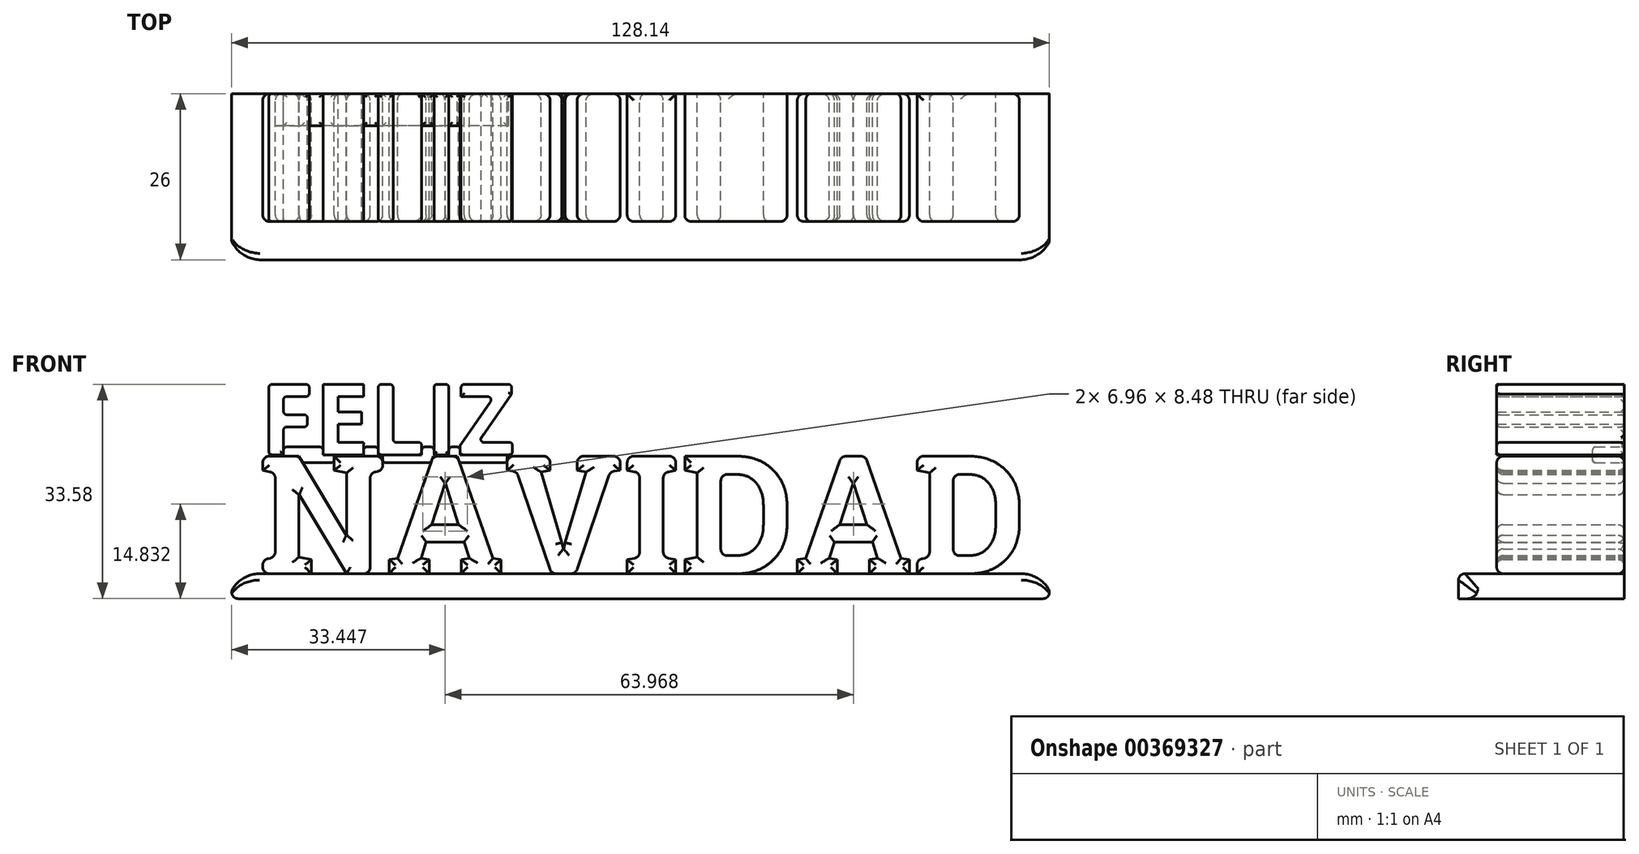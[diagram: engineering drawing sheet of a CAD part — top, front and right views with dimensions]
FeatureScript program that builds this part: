
annotation { "Feature Type Name" : "Feature", "Feature Type Description" : "" }
export const myFeature = defineFeature(function(context is Context, id is Id, definition is map)
    precondition{}
    {
        {
            var Q0;
            Q0=qCreatedBy(makeId("Front.planeOp"),FACE);
            var sketch = newSketch(context, id + "F0", { "sketchPlane" : qUnion([Q0])});
            skText(sketch, "E0", { "text": "NAVIDAD", "fontName": "RobotoSlab-Bold.ttf"});
            skText(sketch, "E1", { "text": "FELIZ", "fontName": "OpenSans-Bold.ttf"});
            skLineSegment(sketch, "E2.bottom", {"start": v(64.02, 0) * mm, "end": v(-65.06, 0) * mm});
            skLineSegment(sketch, "E2.top", {"start": v(64.02, -3.91) * mm, "end": v(-65.06, -3.91) * mm});
            skLineSegment(sketch, "E2.left", {"start": v(64.02, 0) * mm, "end": v(64.02, -3.91) * mm});
            skLineSegment(sketch, "E2.right", {"start": v(-65.06, 0) * mm, "end": v(-65.06, -3.91) * mm});
            skLineSegment(sketch, "E3.bottom", {"start": v(-21.18, 19.85) * mm, "end": v(-57.76, 19.85) * mm});
            skLineSegment(sketch, "E3.top", {"start": v(-21.18, 17.37) * mm, "end": v(-57.76, 17.37) * mm});
            skLineSegment(sketch, "E3.left", {"start": v(-21.18, 19.85) * mm, "end": v(-21.18, 17.37) * mm});
            skLineSegment(sketch, "E3.right", {"start": v(-57.76, 19.85) * mm, "end": v(-57.76, 17.37) * mm});
            const initialGuessF0  = {"E0": [-0.06043, 0, 1, 0, 0.01863], "E1": [-0.06016, 0.01863, 1, 0, 0.01113]};
            skSetInitialGuess(sketch, initialGuessF0);
            skSolve(sketch);
        }
        {
            var Q0;
            Q0=makeQuery(id+"F0.imprint","IMPRINT",FACE,{"disambiguationData":[TD([[makeQuery(id+"F0.imprint","IMPRINT",EDGE,{"derivedFrom":sQuery(id+"F0.wireOp",EDGE,"E0.sketch_text.stroke-115")}),-1.0]])]});
            var Q1;
            Q1=makeQuery(id+"F0.imprint","IMPRINT",FACE,{"disambiguationData":[TD([[makeQuery(id+"F0.imprint","IMPRINT",EDGE,{"derivedFrom":sQuery(id+"F0.wireOp",EDGE,"E0.sketch_text.stroke-95")}),-1.0]])]});
            var Q2;
            Q2=makeQuery(id+"F0.imprint","IMPRINT",FACE,{"disambiguationData":[TD([[makeQuery(id+"F0.imprint","IMPRINT",EDGE,{"derivedFrom":sQuery(id+"F0.wireOp",EDGE,"E0.sketch_text.stroke-74")}),-1.0]])]});
            var Q3;
            Q3=makeQuery(id+"F0.imprint","IMPRINT",FACE,{"disambiguationData":[TD([[makeQuery(id+"F0.imprint","IMPRINT",EDGE,{"derivedFrom":sQuery(id+"F0.wireOp",EDGE,"E0.sketch_text.stroke-62")}),-1.0]])]});
            var Q4;
            Q4=makeQuery(id+"F0.imprint","IMPRINT",FACE,{"disambiguationData":[TD([[makeQuery(id+"F0.imprint","IMPRINT",EDGE,{"derivedFrom":sQuery(id+"F0.wireOp",EDGE,"E0.sketch_text.stroke-44")}),-1.0]])]});
            var Q5;
            {var subQ7=sQuery(id+"F0.wireOp",EDGE,"E0.sketch_text.stroke-24");Q5=makeQuery(id+"F0.imprint","IMPRINT",FACE,{"disambiguationData":[TD([[makeQuery(id+"F0.imprint","IMPRINT",EDGE,{"derivedFrom":subQ7}),-1.0]])]});}
            var Q6;
            {var subQ16=sQuery(id+"F0.wireOp",EDGE,"E0.sketch_text.stroke-1");Q6=makeQuery(id+"F0.imprint","IMPRINT",FACE,{"disambiguationData":[TD([[makeQuery(id+"F0.imprint","IMPRINT",EDGE,{"derivedFrom":subQ16}),-1.0]])]});}
            var Q7;
            {var subQ4=sQuery(id+"F0.wireOp",EDGE,"E1.sketch_text.stroke-1");Q7=makeQuery(id+"F0.imprint","IMPRINT",FACE,{"disambiguationData":[TD([[makeQuery(id+"F0.imprint","IMPRINT",EDGE,{"derivedFrom":subQ4}),-1.0]])]});}
            var Q8;
            {var subQ0=sQuery(id+"F0.wireOp",EDGE,"E1.sketch_text.stroke-9");var subQ1=sQuery(id+"F0.wireOp",EDGE,"E1.sketch_text.stroke-0");var subQ2=makeQuery(id+"F0.imprint","INTERSECT",VERTEX,{"derivedFrom":[subQ1,subQ0]});Q8=makeQuery(id+"F0.imprint","IMPRINT",FACE,{"disambiguationData":[TD([[makeQuery(id+"F0.imprint","IMPRINT",EDGE,{"disambiguationData":[TD([[subQ2,-1.0]])],"derivedFrom":subQ1}),-1.0]])]});}
            var Q9;
            {var subQ0=sQuery(id+"F0.wireOp",EDGE,"E1.sketch_text.stroke-10");Q9=makeQuery(id+"F0.imprint","IMPRINT",FACE,{"disambiguationData":[TD([[makeQuery(id+"F0.imprint","IMPRINT",EDGE,{"derivedFrom":subQ0}),-1.0]])]});}
            var Q10;
            {var subQ1=sQuery(id+"F0.wireOp",EDGE,"E1.sketch_text.stroke-12");Q10=makeQuery(id+"F0.imprint","IMPRINT",FACE,{"disambiguationData":[TD([[makeQuery(id+"F0.imprint","IMPRINT",EDGE,{"derivedFrom":subQ1}),-1.0]])]});}
            var Q11;
            {var subQ1=sQuery(id+"F0.wireOp",EDGE,"E1.sketch_text.stroke-23");Q11=makeQuery(id+"F0.imprint","IMPRINT",FACE,{"disambiguationData":[TD([[makeQuery(id+"F0.imprint","IMPRINT",EDGE,{"derivedFrom":subQ1}),-1.0]])]});}
            var Q12;
            {var subQ0=sQuery(id+"F0.wireOp",EDGE,"E1.sketch_text.stroke-27");Q12=makeQuery(id+"F0.imprint","IMPRINT",FACE,{"disambiguationData":[TD([[makeQuery(id+"F0.imprint","IMPRINT",EDGE,{"derivedFrom":subQ0}),-1.0]])]});}
            var Q13;
            {var subQ0=sQuery(id+"F0.wireOp",EDGE,"E1.sketch_text.stroke-31");Q13=makeQuery(id+"F0.imprint","IMPRINT",FACE,{"disambiguationData":[TD([[makeQuery(id+"F0.imprint","IMPRINT",EDGE,{"derivedFrom":subQ0}),-1.0]])]});}
            var Q14;
            {var subQ0=sQuery(id+"F0.wireOp",EDGE,"E1.sketch_text.stroke-29");Q14=makeQuery(id+"F0.imprint","IMPRINT",FACE,{"disambiguationData":[TD([[makeQuery(id+"F0.imprint","IMPRINT",EDGE,{"derivedFrom":subQ0}),-1.0]])]});}
            var Q15;
            {var subQ0=sQuery(id+"F0.wireOp",EDGE,"E1.sketch_text.stroke-33");var subQ1=sQuery(id+"F0.wireOp",EDGE,"E1.sketch_text.stroke-32");var subQ2=makeQuery(id+"F0.imprint","INTERSECT",VERTEX,{"derivedFrom":[subQ1,subQ0]});Q15=makeQuery(id+"F0.imprint","IMPRINT",FACE,{"disambiguationData":[TD([[makeQuery(id+"F0.imprint","IMPRINT",EDGE,{"disambiguationData":[TD([[subQ2,1.0]])],"derivedFrom":subQ1}),-1.0]])]});}
            var Q16;
            {var subQ6=sQuery(id+"F0.wireOp",EDGE,"E1.sketch_text.stroke-34");Q16=makeQuery(id+"F0.imprint","IMPRINT",FACE,{"disambiguationData":[TD([[makeQuery(id+"F0.imprint","IMPRINT",EDGE,{"derivedFrom":subQ6}),-1.0]])]});}
            var Q17;
            {var subQ0=sQuery(id+"F0.wireOp",EDGE,"E0.sketch_text.stroke-60");var subQ1=sQuery(id+"F0.wireOp",EDGE,"E0.sketch_text.stroke-59");var subQ2=makeQuery(id+"F0.imprint","INTERSECT",VERTEX,{"derivedFrom":[subQ1,subQ0]});Q17=makeQuery(id+"F0.imprint","IMPRINT",FACE,{"disambiguationData":[TD([[makeQuery(id+"F0.imprint","IMPRINT",EDGE,{"disambiguationData":[TD([[subQ2,1.0]])],"derivedFrom":subQ1}),-1.0]])]});}
            var Q18;
            {var subQ0=sQuery(id+"F0.wireOp",EDGE,"E0.sketch_text.stroke-26");Q18=makeQuery(id+"F0.imprint","IMPRINT",FACE,{"disambiguationData":[TD([[makeQuery(id+"F0.imprint","IMPRINT",EDGE,{"derivedFrom":subQ0}),-1.0]])]});}
            var Q19;
            {var subQ0=sQuery(id+"F0.wireOp",EDGE,"E0.sketch_text.stroke-22");Q19=makeQuery(id+"F0.imprint","IMPRINT",FACE,{"disambiguationData":[TD([[makeQuery(id+"F0.imprint","IMPRINT",EDGE,{"derivedFrom":subQ0}),-1.0]])]});}
            var Q20;
            {var subQ0=sQuery(id+"F0.wireOp",EDGE,"E0.sketch_text.stroke-17");var subQ1=sQuery(id+"F0.wireOp",EDGE,"E0.sketch_text.stroke-16");var subQ2=makeQuery(id+"F0.imprint","INTERSECT",VERTEX,{"derivedFrom":[subQ1,subQ0]});Q20=makeQuery(id+"F0.imprint","IMPRINT",FACE,{"disambiguationData":[TD([[makeQuery(id+"F0.imprint","IMPRINT",EDGE,{"disambiguationData":[TD([[subQ2,1.0]])],"derivedFrom":subQ1}),-1.0]])]});}
            extrude(context, id + "F1", {"entities" : qUnion([Q0, Q1, Q2, Q3, Q4, Q5, Q6, Q7, Q8, Q9, Q10, Q11, Q12, Q13, Q14, Q15, Q16, Q17, Q18, Q19, Q20]), "depth" : 20 * mm});
        }
        {
            var Q0;
            {var subQ39=sQuery(id+"F0.wireOp",EDGE,"E0.sketch_text.stroke-22");Q0=makeQuery(id+"F0.imprint","IMPRINT",FACE,{"disambiguationData":[TD([[makeQuery(id+"F0.imprint","IMPRINT",EDGE,{"derivedFrom":subQ39}),1.0]])]});}
            extrude(context, id + "F2", {"entities" : qUnion([Q0]), "depth" : 5 * mm});
        }
        {
            var Q0;
            Q0=makeQuery(id+"F0.imprint","IMPRINT",FACE,{"disambiguationData":[TD([[makeQuery(id+"F0.imprint","IMPRINT",EDGE,{"derivedFrom":sQuery(id+"F0.wireOp",EDGE,"E2.top")}),-1.0]])]});
            extrude(context, id + "F3", {"entities" : qUnion([Q0]), "depth" : 26 * mm});
        }
        {
            var Q0;
            Q0=makeQuery(id+"F3.opExtrude","CAP_EDGE",EDGE,{"disambiguationData":[OSD([sQuery(id+"F0.wireOp",EDGE,"E2.right")])],"isStart":false});
            var Q1;
            Q1=makeQuery(id+"F3.opExtrude","SWEPT_EDGE",EDGE,{"disambiguationData":[OSD([sQuery(id+"F0.wireOp",EDGE,"E2.bottom"),sQuery(id+"F0.wireOp",EDGE,"E2.right")])]});
            var Q2;
            Q2=makeQuery(id+"F3.opExtrude","CAP_EDGE",EDGE,{"disambiguationData":[OSD([sQuery(id+"F0.wireOp",EDGE,"E2.left")])],"isStart":false});
            var Q3;
            Q3=makeQuery(id+"F3.opExtrude","SWEPT_EDGE",EDGE,{"disambiguationData":[OSD([sQuery(id+"F0.wireOp",EDGE,"E2.bottom"),sQuery(id+"F0.wireOp",EDGE,"E2.left")])]});
            fillet(context, id + "F4", {"entities" : qUnion([Q0, Q1, Q2, Q3]), "radius" : 5 * mm, "tangentPropagation" : true, "allowEdgeOverflow" : false});
        }
        {
            var Q0;
            Q0=makeQuery(id+"F1.opExtrude","CAP_FACE",FACE,{"disambiguationData":[OSD([sQuery(id+"F0.wireOp",EDGE,"E0.sketch_text.stroke-0"),sQuery(id+"F0.wireOp",EDGE,"E0.sketch_text.stroke-1"),sQuery(id+"F0.wireOp",EDGE,"E0.sketch_text.stroke-2"),sQuery(id+"F0.wireOp",EDGE,"E0.sketch_text.stroke-4"),sQuery(id+"F0.wireOp",EDGE,"E0.sketch_text.stroke-5"),sQuery(id+"F0.wireOp",EDGE,"E0.sketch_text.stroke-6"),sQuery(id+"F0.wireOp",EDGE,"E0.sketch_text.stroke-7"),sQuery(id+"F0.wireOp",EDGE,"E0.sketch_text.stroke-8"),sQuery(id+"F0.wireOp",EDGE,"E0.sketch_text.stroke-10"),sQuery(id+"F0.wireOp",EDGE,"E0.sketch_text.stroke-11"),sQuery(id+"F0.wireOp",EDGE,"E0.sketch_text.stroke-12"),sQuery(id+"F0.wireOp",EDGE,"E0.sketch_text.stroke-13"),sQuery(id+"F0.wireOp",EDGE,"E0.sketch_text.stroke-14"),sQuery(id+"F0.wireOp",EDGE,"E0.sketch_text.stroke-15"),sQuery(id+"F0.wireOp",EDGE,"E0.sketch_text.stroke-16"),sQuery(id+"F0.wireOp",EDGE,"E0.sketch_text.stroke-17"),sQuery(id+"F0.wireOp",EDGE,"E0.sketch_text.stroke-18"),sQuery(id+"F0.wireOp",EDGE,"E0.sketch_text.stroke-19"),sQuery(id+"F0.wireOp",EDGE,"E0.sketch_text.stroke-20"),sQuery(id+"F0.wireOp",EDGE,"E0.sketch_text.stroke-21"),sQuery(id+"F0.wireOp",EDGE,"E0.sketch_text.stroke-22"),sQuery(id+"F0.wireOp",EDGE,"E0.sketch_text.stroke-23"),sQuery(id+"F0.wireOp",EDGE,"E2.bottom")])],"isStart":false});
            var Q1;
            Q1=makeQuery(id+"F1.opExtrude","CAP_FACE",FACE,{"disambiguationData":[OSD([sQuery(id+"F0.wireOp",EDGE,"E0.sketch_text.stroke-24"),sQuery(id+"F0.wireOp",EDGE,"E0.sketch_text.stroke-25"),sQuery(id+"F0.wireOp",EDGE,"E0.sketch_text.stroke-26"),sQuery(id+"F0.wireOp",EDGE,"E0.sketch_text.stroke-27"),sQuery(id+"F0.wireOp",EDGE,"E0.sketch_text.stroke-28"),sQuery(id+"F0.wireOp",EDGE,"E0.sketch_text.stroke-29"),sQuery(id+"F0.wireOp",EDGE,"E0.sketch_text.stroke-31"),sQuery(id+"F0.wireOp",EDGE,"E0.sketch_text.stroke-32"),sQuery(id+"F0.wireOp",EDGE,"E0.sketch_text.stroke-33"),sQuery(id+"F0.wireOp",EDGE,"E0.sketch_text.stroke-34"),sQuery(id+"F0.wireOp",EDGE,"E0.sketch_text.stroke-35"),sQuery(id+"F0.wireOp",EDGE,"E0.sketch_text.stroke-36"),sQuery(id+"F0.wireOp",EDGE,"E0.sketch_text.stroke-37"),sQuery(id+"F0.wireOp",EDGE,"E0.sketch_text.stroke-39"),sQuery(id+"F0.wireOp",EDGE,"E0.sketch_text.stroke-40"),sQuery(id+"F0.wireOp",EDGE,"E0.sketch_text.stroke-41"),sQuery(id+"F0.wireOp",EDGE,"E0.sketch_text.stroke-42"),sQuery(id+"F0.wireOp",EDGE,"E0.sketch_text.stroke-43"),sQuery(id+"F0.wireOp",EDGE,"E2.bottom")])],"isStart":false});
            var Q2;
            Q2=makeQuery(id+"F1.opExtrude","CAP_FACE",FACE,{"disambiguationData":[OSD([sQuery(id+"F0.wireOp",EDGE,"E0.sketch_text.stroke-44"),sQuery(id+"F0.wireOp",EDGE,"E0.sketch_text.stroke-45"),sQuery(id+"F0.wireOp",EDGE,"E0.sketch_text.stroke-46"),sQuery(id+"F0.wireOp",EDGE,"E0.sketch_text.stroke-47"),sQuery(id+"F0.wireOp",EDGE,"E0.sketch_text.stroke-48"),sQuery(id+"F0.wireOp",EDGE,"E0.sketch_text.stroke-49"),sQuery(id+"F0.wireOp",EDGE,"E0.sketch_text.stroke-50"),sQuery(id+"F0.wireOp",EDGE,"E0.sketch_text.stroke-51"),sQuery(id+"F0.wireOp",EDGE,"E0.sketch_text.stroke-52"),sQuery(id+"F0.wireOp",EDGE,"E0.sketch_text.stroke-53"),sQuery(id+"F0.wireOp",EDGE,"E0.sketch_text.stroke-54"),sQuery(id+"F0.wireOp",EDGE,"E0.sketch_text.stroke-55"),sQuery(id+"F0.wireOp",EDGE,"E0.sketch_text.stroke-57"),sQuery(id+"F0.wireOp",EDGE,"E0.sketch_text.stroke-58"),sQuery(id+"F0.wireOp",EDGE,"E0.sketch_text.stroke-59"),sQuery(id+"F0.wireOp",EDGE,"E0.sketch_text.stroke-60"),sQuery(id+"F0.wireOp",EDGE,"E0.sketch_text.stroke-61"),sQuery(id+"F0.wireOp",EDGE,"E2.bottom")])],"isStart":false});
            var Q3;
            Q3=makeQuery(id+"F1.opExtrude","CAP_FACE",FACE,{"disambiguationData":[OSD([sQuery(id+"F0.wireOp",EDGE,"E0.sketch_text.stroke-62"),sQuery(id+"F0.wireOp",EDGE,"E0.sketch_text.stroke-63"),sQuery(id+"F0.wireOp",EDGE,"E0.sketch_text.stroke-64"),sQuery(id+"F0.wireOp",EDGE,"E0.sketch_text.stroke-65"),sQuery(id+"F0.wireOp",EDGE,"E0.sketch_text.stroke-66"),sQuery(id+"F0.wireOp",EDGE,"E0.sketch_text.stroke-67"),sQuery(id+"F0.wireOp",EDGE,"E0.sketch_text.stroke-68"),sQuery(id+"F0.wireOp",EDGE,"E0.sketch_text.stroke-70"),sQuery(id+"F0.wireOp",EDGE,"E0.sketch_text.stroke-71"),sQuery(id+"F0.wireOp",EDGE,"E0.sketch_text.stroke-72"),sQuery(id+"F0.wireOp",EDGE,"E0.sketch_text.stroke-73"),sQuery(id+"F0.wireOp",EDGE,"E2.bottom")])],"isStart":false});
            var Q4;
            Q4=makeQuery(id+"F1.opExtrude","CAP_FACE",FACE,{"disambiguationData":[OSD([sQuery(id+"F0.wireOp",EDGE,"E0.sketch_text.stroke-74"),sQuery(id+"F0.wireOp",EDGE,"E0.sketch_text.stroke-75"),sQuery(id+"F0.wireOp",EDGE,"E0.sketch_text.stroke-76"),sQuery(id+"F0.wireOp",EDGE,"E0.sketch_text.stroke-77"),sQuery(id+"F0.wireOp",EDGE,"E0.sketch_text.stroke-78"),sQuery(id+"F0.wireOp",EDGE,"E0.sketch_text.stroke-80"),sQuery(id+"F0.wireOp",EDGE,"E0.sketch_text.stroke-81"),sQuery(id+"F0.wireOp",EDGE,"E0.sketch_text.stroke-82"),sQuery(id+"F0.wireOp",EDGE,"E0.sketch_text.stroke-83"),sQuery(id+"F0.wireOp",EDGE,"E0.sketch_text.stroke-84"),sQuery(id+"F0.wireOp",EDGE,"E0.sketch_text.stroke-85"),sQuery(id+"F0.wireOp",EDGE,"E0.sketch_text.stroke-86"),sQuery(id+"F0.wireOp",EDGE,"E0.sketch_text.stroke-87"),sQuery(id+"F0.wireOp",EDGE,"E0.sketch_text.stroke-88"),sQuery(id+"F0.wireOp",EDGE,"E0.sketch_text.stroke-89"),sQuery(id+"F0.wireOp",EDGE,"E0.sketch_text.stroke-90"),sQuery(id+"F0.wireOp",EDGE,"E0.sketch_text.stroke-91"),sQuery(id+"F0.wireOp",EDGE,"E0.sketch_text.stroke-92"),sQuery(id+"F0.wireOp",EDGE,"E0.sketch_text.stroke-93"),sQuery(id+"F0.wireOp",EDGE,"E0.sketch_text.stroke-94"),sQuery(id+"F0.wireOp",EDGE,"E2.bottom")])],"isStart":false});
            var Q5;
            Q5=makeQuery(id+"F1.opExtrude","CAP_FACE",FACE,{"disambiguationData":[OSD([sQuery(id+"F0.wireOp",EDGE,"E0.sketch_text.stroke-95"),sQuery(id+"F0.wireOp",EDGE,"E0.sketch_text.stroke-96"),sQuery(id+"F0.wireOp",EDGE,"E0.sketch_text.stroke-97"),sQuery(id+"F0.wireOp",EDGE,"E0.sketch_text.stroke-98"),sQuery(id+"F0.wireOp",EDGE,"E0.sketch_text.stroke-99"),sQuery(id+"F0.wireOp",EDGE,"E0.sketch_text.stroke-100"),sQuery(id+"F0.wireOp",EDGE,"E0.sketch_text.stroke-102"),sQuery(id+"F0.wireOp",EDGE,"E0.sketch_text.stroke-103"),sQuery(id+"F0.wireOp",EDGE,"E0.sketch_text.stroke-104"),sQuery(id+"F0.wireOp",EDGE,"E0.sketch_text.stroke-105"),sQuery(id+"F0.wireOp",EDGE,"E0.sketch_text.stroke-106"),sQuery(id+"F0.wireOp",EDGE,"E0.sketch_text.stroke-107"),sQuery(id+"F0.wireOp",EDGE,"E0.sketch_text.stroke-108"),sQuery(id+"F0.wireOp",EDGE,"E0.sketch_text.stroke-110"),sQuery(id+"F0.wireOp",EDGE,"E0.sketch_text.stroke-111"),sQuery(id+"F0.wireOp",EDGE,"E0.sketch_text.stroke-112"),sQuery(id+"F0.wireOp",EDGE,"E0.sketch_text.stroke-113"),sQuery(id+"F0.wireOp",EDGE,"E0.sketch_text.stroke-114"),sQuery(id+"F0.wireOp",EDGE,"E2.bottom")])],"isStart":false});
            var Q6;
            Q6=makeQuery(id+"F1.opExtrude","CAP_FACE",FACE,{"disambiguationData":[OSD([sQuery(id+"F0.wireOp",EDGE,"E0.sketch_text.stroke-115"),sQuery(id+"F0.wireOp",EDGE,"E0.sketch_text.stroke-116"),sQuery(id+"F0.wireOp",EDGE,"E0.sketch_text.stroke-117"),sQuery(id+"F0.wireOp",EDGE,"E0.sketch_text.stroke-118"),sQuery(id+"F0.wireOp",EDGE,"E0.sketch_text.stroke-119"),sQuery(id+"F0.wireOp",EDGE,"E0.sketch_text.stroke-121"),sQuery(id+"F0.wireOp",EDGE,"E0.sketch_text.stroke-122"),sQuery(id+"F0.wireOp",EDGE,"E0.sketch_text.stroke-123"),sQuery(id+"F0.wireOp",EDGE,"E0.sketch_text.stroke-124"),sQuery(id+"F0.wireOp",EDGE,"E0.sketch_text.stroke-125"),sQuery(id+"F0.wireOp",EDGE,"E0.sketch_text.stroke-126"),sQuery(id+"F0.wireOp",EDGE,"E0.sketch_text.stroke-127"),sQuery(id+"F0.wireOp",EDGE,"E0.sketch_text.stroke-128"),sQuery(id+"F0.wireOp",EDGE,"E0.sketch_text.stroke-129"),sQuery(id+"F0.wireOp",EDGE,"E0.sketch_text.stroke-130"),sQuery(id+"F0.wireOp",EDGE,"E0.sketch_text.stroke-131"),sQuery(id+"F0.wireOp",EDGE,"E0.sketch_text.stroke-132"),sQuery(id+"F0.wireOp",EDGE,"E0.sketch_text.stroke-133"),sQuery(id+"F0.wireOp",EDGE,"E0.sketch_text.stroke-134"),sQuery(id+"F0.wireOp",EDGE,"E0.sketch_text.stroke-135"),sQuery(id+"F0.wireOp",EDGE,"E2.bottom")])],"isStart":false});
            var Q7;
            Q7=makeQuery(id+"F1.opExtrude","SWEPT_FACE",FACE,{"disambiguationData":[OSD([sQuery(id+"F0.wireOp",EDGE,"E0.sketch_text.stroke-15"),sQuery(id+"F0.wireOp",EDGE,"E0.sketch_text.stroke-16")])]});
            var Q8;
            Q8=makeQuery(id+"F1.opExtrude","SWEPT_FACE",FACE,{"disambiguationData":[OSD([sQuery(id+"F0.wireOp",EDGE,"E0.sketch_text.stroke-2")])]});
            var Q9;
            Q9=makeQuery(id+"F1.opExtrude","SWEPT_FACE",FACE,{"disambiguationData":[OSD([sQuery(id+"F0.wireOp",EDGE,"E0.sketch_text.stroke-12")])]});
            var Q10;
            Q10=makeQuery(id+"F1.opExtrude","SWEPT_FACE",FACE,{"disambiguationData":[OSD([sQuery(id+"F0.wireOp",EDGE,"E0.sketch_text.stroke-10")])]});
            var Q11;
            Q11=makeQuery(id+"F1.opExtrude","SWEPT_FACE",FACE,{"disambiguationData":[OSD([sQuery(id+"F0.wireOp",EDGE,"E0.sketch_text.stroke-0")])]});
            var Q12;
            Q12=makeQuery(id+"F1.opExtrude","SWEPT_FACE",FACE,{"disambiguationData":[OSD([sQuery(id+"F0.wireOp",EDGE,"E0.sketch_text.stroke-26")])]});
            var Q13;
            Q13=makeQuery(id+"F1.opExtrude","SWEPT_FACE",FACE,{"disambiguationData":[OSD([sQuery(id+"F0.wireOp",EDGE,"E0.sketch_text.stroke-60")])]});
            var Q14;
            Q14=makeQuery(id+"F1.opExtrude","SWEPT_FACE",FACE,{"disambiguationData":[OSD([sQuery(id+"F0.wireOp",EDGE,"E0.sketch_text.stroke-52")])]});
            var Q15;
            Q15=makeQuery(id+"F1.opExtrude","SWEPT_FACE",FACE,{"disambiguationData":[OSD([sQuery(id+"F0.wireOp",EDGE,"E0.sketch_text.stroke-63")])]});
            var Q16;
            Q16=makeQuery(id+"F1.opExtrude","SWEPT_FACE",FACE,{"disambiguationData":[OSD([sQuery(id+"F0.wireOp",EDGE,"E0.sketch_text.stroke-97")])]});
            var Q17;
            Q17=makeQuery(id+"F1.opExtrude","SWEPT_FACE",FACE,{"disambiguationData":[OSD([sQuery(id+"F0.wireOp",EDGE,"E0.sketch_text.stroke-126"),sQuery(id+"F0.wireOp",EDGE,"E0.sketch_text.stroke-127")])]});
            var Q18;
            Q18=makeQuery(id+"F1.opExtrude","SWEPT_FACE",FACE,{"disambiguationData":[OSD([sQuery(id+"F0.wireOp",EDGE,"E0.sketch_text.stroke-122")])]});
            var Q19;
            Q19=makeQuery(id+"F1.opExtrude","SWEPT_FACE",FACE,{"disambiguationData":[OSD([sQuery(id+"F0.wireOp",EDGE,"E0.sketch_text.stroke-87")])]});
            var Q20;
            Q20=makeQuery(id+"F1.opExtrude","SWEPT_FACE",FACE,{"disambiguationData":[OSD([sQuery(id+"F0.wireOp",EDGE,"E0.sketch_text.stroke-128")])]});
            var Q21;
            {var subQ0=sQuery(id+"F0.wireOp",EDGE,"E2.left");Q21=makeQuery(id+"F4.opFillet","BLEND_EDGE",EDGE,{"blendedFrom":[makeQuery(id+"F3.opExtrude","SWEPT_EDGE",EDGE,{"disambiguationData":[OSD([sQuery(id+"F0.wireOp",EDGE,"E2.bottom"),subQ0])]}),makeQuery(id+"F3.opExtrude","CAP_EDGE",EDGE,{"disambiguationData":[OSD([subQ0])],"isStart":false})],"blendedInto":[]});}
            var Q22;
            Q22=makeQuery(id+"F1.opExtrude","SWEPT_FACE",FACE,{"disambiguationData":[OSD([sQuery(id+"F0.wireOp",EDGE,"E0.sketch_text.stroke-72")])]});
            var Q23;
            Q23=makeQuery(id+"F1.opExtrude","SWEPT_FACE",FACE,{"disambiguationData":[OSD([sQuery(id+"F0.wireOp",EDGE,"E0.sketch_text.stroke-66")])]});
            var Q24;
            Q24=makeQuery(id+"F1.opExtrude","SWEPT_FACE",FACE,{"disambiguationData":[OSD([sQuery(id+"F0.wireOp",EDGE,"E0.sketch_text.stroke-55")])]});
            var Q25;
            Q25=makeQuery(id+"F1.opExtrude","SWEPT_FACE",FACE,{"disambiguationData":[OSD([sQuery(id+"F0.wireOp",EDGE,"E0.sketch_text.stroke-57")])]});
            var Q26;
            Q26=makeQuery(id+"F1.opExtrude","CAP_FACE",FACE,{"disambiguationData":[OSD([sQuery(id+"F0.wireOp",EDGE,"E0.sketch_text.stroke-95"),sQuery(id+"F0.wireOp",EDGE,"E0.sketch_text.stroke-96"),sQuery(id+"F0.wireOp",EDGE,"E0.sketch_text.stroke-97"),sQuery(id+"F0.wireOp",EDGE,"E0.sketch_text.stroke-98"),sQuery(id+"F0.wireOp",EDGE,"E0.sketch_text.stroke-99"),sQuery(id+"F0.wireOp",EDGE,"E0.sketch_text.stroke-100"),sQuery(id+"F0.wireOp",EDGE,"E0.sketch_text.stroke-102"),sQuery(id+"F0.wireOp",EDGE,"E0.sketch_text.stroke-103"),sQuery(id+"F0.wireOp",EDGE,"E0.sketch_text.stroke-104"),sQuery(id+"F0.wireOp",EDGE,"E0.sketch_text.stroke-105"),sQuery(id+"F0.wireOp",EDGE,"E0.sketch_text.stroke-106"),sQuery(id+"F0.wireOp",EDGE,"E0.sketch_text.stroke-107"),sQuery(id+"F0.wireOp",EDGE,"E0.sketch_text.stroke-108"),sQuery(id+"F0.wireOp",EDGE,"E0.sketch_text.stroke-110"),sQuery(id+"F0.wireOp",EDGE,"E0.sketch_text.stroke-111"),sQuery(id+"F0.wireOp",EDGE,"E0.sketch_text.stroke-112"),sQuery(id+"F0.wireOp",EDGE,"E0.sketch_text.stroke-113"),sQuery(id+"F0.wireOp",EDGE,"E0.sketch_text.stroke-114"),sQuery(id+"F0.wireOp",EDGE,"E2.bottom")])],"isStart":true});
            var Q27;
            Q27=makeQuery(id+"F1.opExtrude","CAP_FACE",FACE,{"disambiguationData":[OSD([sQuery(id+"F0.wireOp",EDGE,"E0.sketch_text.stroke-24"),sQuery(id+"F0.wireOp",EDGE,"E0.sketch_text.stroke-25"),sQuery(id+"F0.wireOp",EDGE,"E0.sketch_text.stroke-26"),sQuery(id+"F0.wireOp",EDGE,"E0.sketch_text.stroke-27"),sQuery(id+"F0.wireOp",EDGE,"E0.sketch_text.stroke-28"),sQuery(id+"F0.wireOp",EDGE,"E0.sketch_text.stroke-29"),sQuery(id+"F0.wireOp",EDGE,"E0.sketch_text.stroke-31"),sQuery(id+"F0.wireOp",EDGE,"E0.sketch_text.stroke-32"),sQuery(id+"F0.wireOp",EDGE,"E0.sketch_text.stroke-33"),sQuery(id+"F0.wireOp",EDGE,"E0.sketch_text.stroke-34"),sQuery(id+"F0.wireOp",EDGE,"E0.sketch_text.stroke-35"),sQuery(id+"F0.wireOp",EDGE,"E0.sketch_text.stroke-36"),sQuery(id+"F0.wireOp",EDGE,"E0.sketch_text.stroke-37"),sQuery(id+"F0.wireOp",EDGE,"E0.sketch_text.stroke-39"),sQuery(id+"F0.wireOp",EDGE,"E0.sketch_text.stroke-40"),sQuery(id+"F0.wireOp",EDGE,"E0.sketch_text.stroke-41"),sQuery(id+"F0.wireOp",EDGE,"E0.sketch_text.stroke-42"),sQuery(id+"F0.wireOp",EDGE,"E0.sketch_text.stroke-43"),sQuery(id+"F0.wireOp",EDGE,"E2.bottom")])],"isStart":true});
            var Q28;
            Q28=makeQuery(id+"F1.opExtrude","CAP_FACE",FACE,{"disambiguationData":[OSD([sQuery(id+"F0.wireOp",EDGE,"E0.sketch_text.stroke-0"),sQuery(id+"F0.wireOp",EDGE,"E0.sketch_text.stroke-1"),sQuery(id+"F0.wireOp",EDGE,"E0.sketch_text.stroke-2"),sQuery(id+"F0.wireOp",EDGE,"E0.sketch_text.stroke-4"),sQuery(id+"F0.wireOp",EDGE,"E0.sketch_text.stroke-5"),sQuery(id+"F0.wireOp",EDGE,"E0.sketch_text.stroke-6"),sQuery(id+"F0.wireOp",EDGE,"E0.sketch_text.stroke-7"),sQuery(id+"F0.wireOp",EDGE,"E0.sketch_text.stroke-8"),sQuery(id+"F0.wireOp",EDGE,"E0.sketch_text.stroke-10"),sQuery(id+"F0.wireOp",EDGE,"E0.sketch_text.stroke-11"),sQuery(id+"F0.wireOp",EDGE,"E0.sketch_text.stroke-12"),sQuery(id+"F0.wireOp",EDGE,"E0.sketch_text.stroke-13"),sQuery(id+"F0.wireOp",EDGE,"E0.sketch_text.stroke-14"),sQuery(id+"F0.wireOp",EDGE,"E0.sketch_text.stroke-15"),sQuery(id+"F0.wireOp",EDGE,"E0.sketch_text.stroke-16"),sQuery(id+"F0.wireOp",EDGE,"E0.sketch_text.stroke-17"),sQuery(id+"F0.wireOp",EDGE,"E0.sketch_text.stroke-18"),sQuery(id+"F0.wireOp",EDGE,"E0.sketch_text.stroke-19"),sQuery(id+"F0.wireOp",EDGE,"E0.sketch_text.stroke-20"),sQuery(id+"F0.wireOp",EDGE,"E0.sketch_text.stroke-21"),sQuery(id+"F0.wireOp",EDGE,"E0.sketch_text.stroke-22"),sQuery(id+"F0.wireOp",EDGE,"E0.sketch_text.stroke-23"),sQuery(id+"F0.wireOp",EDGE,"E2.bottom")])],"isStart":true});
            var Q29;
            Q29=makeQuery(id+"F1.opExtrude","CAP_FACE",FACE,{"disambiguationData":[OSD([sQuery(id+"F0.wireOp",EDGE,"E0.sketch_text.stroke-44"),sQuery(id+"F0.wireOp",EDGE,"E0.sketch_text.stroke-45"),sQuery(id+"F0.wireOp",EDGE,"E0.sketch_text.stroke-46"),sQuery(id+"F0.wireOp",EDGE,"E0.sketch_text.stroke-47"),sQuery(id+"F0.wireOp",EDGE,"E0.sketch_text.stroke-48"),sQuery(id+"F0.wireOp",EDGE,"E0.sketch_text.stroke-49"),sQuery(id+"F0.wireOp",EDGE,"E0.sketch_text.stroke-50"),sQuery(id+"F0.wireOp",EDGE,"E0.sketch_text.stroke-51"),sQuery(id+"F0.wireOp",EDGE,"E0.sketch_text.stroke-52"),sQuery(id+"F0.wireOp",EDGE,"E0.sketch_text.stroke-53"),sQuery(id+"F0.wireOp",EDGE,"E0.sketch_text.stroke-54"),sQuery(id+"F0.wireOp",EDGE,"E0.sketch_text.stroke-55"),sQuery(id+"F0.wireOp",EDGE,"E0.sketch_text.stroke-57"),sQuery(id+"F0.wireOp",EDGE,"E0.sketch_text.stroke-58"),sQuery(id+"F0.wireOp",EDGE,"E0.sketch_text.stroke-59"),sQuery(id+"F0.wireOp",EDGE,"E0.sketch_text.stroke-60"),sQuery(id+"F0.wireOp",EDGE,"E0.sketch_text.stroke-61"),sQuery(id+"F0.wireOp",EDGE,"E2.bottom")])],"isStart":true});
            var Q30;
            Q30=makeQuery(id+"F1.opExtrude","CAP_FACE",FACE,{"disambiguationData":[OSD([sQuery(id+"F0.wireOp",EDGE,"E0.sketch_text.stroke-24"),sQuery(id+"F0.wireOp",EDGE,"E0.sketch_text.stroke-25"),sQuery(id+"F0.wireOp",EDGE,"E0.sketch_text.stroke-26"),sQuery(id+"F0.wireOp",EDGE,"E0.sketch_text.stroke-27"),sQuery(id+"F0.wireOp",EDGE,"E0.sketch_text.stroke-28"),sQuery(id+"F0.wireOp",EDGE,"E0.sketch_text.stroke-29"),sQuery(id+"F0.wireOp",EDGE,"E0.sketch_text.stroke-31"),sQuery(id+"F0.wireOp",EDGE,"E0.sketch_text.stroke-32"),sQuery(id+"F0.wireOp",EDGE,"E0.sketch_text.stroke-33"),sQuery(id+"F0.wireOp",EDGE,"E0.sketch_text.stroke-34"),sQuery(id+"F0.wireOp",EDGE,"E0.sketch_text.stroke-35"),sQuery(id+"F0.wireOp",EDGE,"E0.sketch_text.stroke-36"),sQuery(id+"F0.wireOp",EDGE,"E0.sketch_text.stroke-37"),sQuery(id+"F0.wireOp",EDGE,"E0.sketch_text.stroke-39"),sQuery(id+"F0.wireOp",EDGE,"E0.sketch_text.stroke-40"),sQuery(id+"F0.wireOp",EDGE,"E0.sketch_text.stroke-41"),sQuery(id+"F0.wireOp",EDGE,"E0.sketch_text.stroke-42"),sQuery(id+"F0.wireOp",EDGE,"E0.sketch_text.stroke-43"),sQuery(id+"F0.wireOp",EDGE,"E2.bottom")])],"isStart":true});
            fillet(context, id + "F5", {"entities" : qUnion([Q0, Q1, Q2, Q3, Q4, Q5, Q6, Q7, Q8, Q9, Q10, Q11, Q12, Q13, Q14, Q15, Q16, Q17, Q18, Q19, Q20, Q21, Q22, Q23, Q24, Q25, Q26, Q27, Q28, Q29, Q30]), "radius" : 1 * mm, "tangentPropagation" : true, "allowEdgeOverflow" : false});
        }
        {
            var Q0;
            Q0=makeQuery(id+"F1.opExtrude","CAP_FACE",FACE,{"disambiguationData":[OSD([sQuery(id+"F0.wireOp",EDGE,"E1.sketch_text.stroke-32"),sQuery(id+"F0.wireOp",EDGE,"E1.sketch_text.stroke-33"),sQuery(id+"F0.wireOp",EDGE,"E1.sketch_text.stroke-34"),sQuery(id+"F0.wireOp",EDGE,"E1.sketch_text.stroke-35"),sQuery(id+"F0.wireOp",EDGE,"E1.sketch_text.stroke-36"),sQuery(id+"F0.wireOp",EDGE,"E1.sketch_text.stroke-37"),sQuery(id+"F0.wireOp",EDGE,"E1.sketch_text.stroke-38"),sQuery(id+"F0.wireOp",EDGE,"E1.sketch_text.stroke-39"),sQuery(id+"F0.wireOp",EDGE,"E1.sketch_text.stroke-40"),sQuery(id+"F0.wireOp",EDGE,"E1.sketch_text.stroke-41")])],"isStart":false});
            var Q1;
            Q1=makeQuery(id+"F1.opExtrude","CAP_FACE",FACE,{"disambiguationData":[OSD([sQuery(id+"F0.wireOp",EDGE,"E1.sketch_text.stroke-28"),sQuery(id+"F0.wireOp",EDGE,"E1.sketch_text.stroke-29"),sQuery(id+"F0.wireOp",EDGE,"E1.sketch_text.stroke-30"),sQuery(id+"F0.wireOp",EDGE,"E1.sketch_text.stroke-31")])],"isStart":false});
            var Q2;
            Q2=makeQuery(id+"F1.opExtrude","CAP_FACE",FACE,{"disambiguationData":[OSD([sQuery(id+"F0.wireOp",EDGE,"E1.sketch_text.stroke-22"),sQuery(id+"F0.wireOp",EDGE,"E1.sketch_text.stroke-23"),sQuery(id+"F0.wireOp",EDGE,"E1.sketch_text.stroke-24"),sQuery(id+"F0.wireOp",EDGE,"E1.sketch_text.stroke-25"),sQuery(id+"F0.wireOp",EDGE,"E1.sketch_text.stroke-26"),sQuery(id+"F0.wireOp",EDGE,"E1.sketch_text.stroke-27")])],"isStart":false});
            var Q3;
            Q3=makeQuery(id+"F1.opExtrude","CAP_FACE",FACE,{"disambiguationData":[OSD([sQuery(id+"F0.wireOp",EDGE,"E1.sketch_text.stroke-10"),sQuery(id+"F0.wireOp",EDGE,"E1.sketch_text.stroke-11"),sQuery(id+"F0.wireOp",EDGE,"E1.sketch_text.stroke-12"),sQuery(id+"F0.wireOp",EDGE,"E1.sketch_text.stroke-13"),sQuery(id+"F0.wireOp",EDGE,"E1.sketch_text.stroke-14"),sQuery(id+"F0.wireOp",EDGE,"E1.sketch_text.stroke-15"),sQuery(id+"F0.wireOp",EDGE,"E1.sketch_text.stroke-16"),sQuery(id+"F0.wireOp",EDGE,"E1.sketch_text.stroke-17"),sQuery(id+"F0.wireOp",EDGE,"E1.sketch_text.stroke-18"),sQuery(id+"F0.wireOp",EDGE,"E1.sketch_text.stroke-19"),sQuery(id+"F0.wireOp",EDGE,"E1.sketch_text.stroke-20"),sQuery(id+"F0.wireOp",EDGE,"E1.sketch_text.stroke-21")])],"isStart":false});
            var Q4;
            Q4=makeQuery(id+"F1.opExtrude","CAP_FACE",FACE,{"disambiguationData":[OSD([sQuery(id+"F0.wireOp",EDGE,"E1.sketch_text.stroke-0"),sQuery(id+"F0.wireOp",EDGE,"E1.sketch_text.stroke-1"),sQuery(id+"F0.wireOp",EDGE,"E1.sketch_text.stroke-2"),sQuery(id+"F0.wireOp",EDGE,"E1.sketch_text.stroke-3"),sQuery(id+"F0.wireOp",EDGE,"E1.sketch_text.stroke-4"),sQuery(id+"F0.wireOp",EDGE,"E1.sketch_text.stroke-5"),sQuery(id+"F0.wireOp",EDGE,"E1.sketch_text.stroke-6"),sQuery(id+"F0.wireOp",EDGE,"E1.sketch_text.stroke-7"),sQuery(id+"F0.wireOp",EDGE,"E1.sketch_text.stroke-8"),sQuery(id+"F0.wireOp",EDGE,"E1.sketch_text.stroke-9")])],"isStart":false});
            var Q5;
            Q5=makeQuery(id+"F1.opExtrude","SWEPT_FACE",FACE,{"disambiguationData":[OSD([sQuery(id+"F0.wireOp",EDGE,"E1.sketch_text.stroke-1")])]});
            var Q6;
            Q6=makeQuery(id+"F1.opExtrude","SWEPT_FACE",FACE,{"disambiguationData":[OSD([sQuery(id+"F0.wireOp",EDGE,"E1.sketch_text.stroke-2")])]});
            var Q7;
            Q7=makeQuery(id+"F1.opExtrude","SWEPT_FACE",FACE,{"disambiguationData":[OSD([sQuery(id+"F0.wireOp",EDGE,"E1.sketch_text.stroke-12")])]});
            var Q8;
            Q8=makeQuery(id+"F1.opExtrude","SWEPT_FACE",FACE,{"disambiguationData":[OSD([sQuery(id+"F0.wireOp",EDGE,"E1.sketch_text.stroke-23")])]});
            var Q9;
            Q9=makeQuery(id+"F1.opExtrude","SWEPT_FACE",FACE,{"disambiguationData":[OSD([sQuery(id+"F0.wireOp",EDGE,"E1.sketch_text.stroke-29")])]});
            var Q10;
            Q10=makeQuery(id+"F1.opExtrude","SWEPT_FACE",FACE,{"disambiguationData":[OSD([sQuery(id+"F0.wireOp",EDGE,"E1.sketch_text.stroke-37")])]});
            var Q11;
            Q11=makeQuery(id+"F1.opExtrude","SWEPT_FACE",FACE,{"disambiguationData":[OSD([sQuery(id+"F0.wireOp",EDGE,"E1.sketch_text.stroke-25")])]});
            var Q12;
            Q12=makeQuery(id+"F1.opExtrude","SWEPT_FACE",FACE,{"disambiguationData":[OSD([sQuery(id+"F0.wireOp",EDGE,"E1.sketch_text.stroke-20")])]});
            var Q13;
            Q13=makeQuery(id+"F1.opExtrude","SWEPT_FACE",FACE,{"disambiguationData":[OSD([sQuery(id+"F0.wireOp",EDGE,"E1.sketch_text.stroke-16")])]});
            var Q14;
            Q14=makeQuery(id+"F1.opExtrude","SWEPT_FACE",FACE,{"disambiguationData":[OSD([sQuery(id+"F0.wireOp",EDGE,"E1.sketch_text.stroke-6")])]});
            var Q15;
            Q15=makeQuery(id+"F1.opExtrude","SWEPT_FACE",FACE,{"disambiguationData":[OSD([sQuery(id+"F0.wireOp",EDGE,"E1.sketch_text.stroke-40")])]});
            var Q16;
            Q16=makeQuery(id+"F1.opExtrude","SWEPT_FACE",FACE,{"disambiguationData":[OSD([sQuery(id+"F0.wireOp",EDGE,"E1.sketch_text.stroke-34")])]});
            var Q17;
            Q17=makeQuery(id+"F1.opExtrude","SWEPT_FACE",FACE,{"disambiguationData":[OSD([sQuery(id+"F0.wireOp",EDGE,"E1.sketch_text.stroke-18")])]});
            var Q18;
            Q18=makeQuery(id+"F1.opExtrude","SWEPT_FACE",FACE,{"disambiguationData":[OSD([sQuery(id+"F0.wireOp",EDGE,"E1.sketch_text.stroke-14")])]});
            var Q19;
            Q19=makeQuery(id+"F1.opExtrude","SWEPT_FACE",FACE,{"disambiguationData":[OSD([sQuery(id+"F0.wireOp",EDGE,"E1.sketch_text.stroke-4")])]});
            var Q20;
            Q20=makeQuery(id+"F1.opExtrude","SWEPT_FACE",FACE,{"disambiguationData":[OSD([sQuery(id+"F0.wireOp",EDGE,"E1.sketch_text.stroke-8")])]});
            var Q21;
            Q21=makeQuery(id+"F1.opExtrude","SWEPT_FACE",FACE,{"disambiguationData":[OSD([sQuery(id+"F0.wireOp",EDGE,"E1.sketch_text.stroke-27")])]});
            var Q22;
            Q22=makeQuery(id+"F1.opExtrude","SWEPT_FACE",FACE,{"disambiguationData":[OSD([sQuery(id+"F0.wireOp",EDGE,"E1.sketch_text.stroke-10")])]});
            var Q23;
            {var subQ0=sQuery(id+"F0.wireOp",EDGE,"E3.bottom");Q23=makeQuery(id+"F2.opExtrude","SWEPT_FACE",FACE,{"disambiguationData":[OSD([subQ0]),TDD([makeQuery(id+"F0.imprint","IMPRINT",EDGE,{"disambiguationData":[TD([[makeQuery(id+"F0.imprint","INTERSECT",VERTEX,{"derivedFrom":[sQuery(id+"F0.wireOp",EDGE,"E1.sketch_text.stroke-9"),subQ0]}),1.0]])],"derivedFrom":subQ0})])]});}
            var Q24;
            {var subQ0=sQuery(id+"F0.wireOp",EDGE,"E3.bottom");Q24=makeQuery(id+"F2.opExtrude","SWEPT_FACE",FACE,{"disambiguationData":[OSD([subQ0]),TDD([makeQuery(id+"F0.imprint","IMPRINT",EDGE,{"disambiguationData":[TD([[makeQuery(id+"F0.imprint","INTERSECT",VERTEX,{"derivedFrom":[sQuery(id+"F0.wireOp",EDGE,"E1.sketch_text.stroke-21"),subQ0]}),1.0]])],"derivedFrom":subQ0})])]});}
            var Q25;
            {var subQ0=sQuery(id+"F0.wireOp",EDGE,"E3.bottom");Q25=makeQuery(id+"F2.opExtrude","SWEPT_FACE",FACE,{"disambiguationData":[OSD([subQ0]),TDD([makeQuery(id+"F0.imprint","IMPRINT",EDGE,{"disambiguationData":[TD([[makeQuery(id+"F0.imprint","INTERSECT",VERTEX,{"derivedFrom":[sQuery(id+"F0.wireOp",EDGE,"E1.sketch_text.stroke-26"),subQ0]}),1.0]])],"derivedFrom":subQ0})])]});}
            var Q26;
            {var subQ0=sQuery(id+"F0.wireOp",EDGE,"E3.bottom");Q26=makeQuery(id+"F2.opExtrude","SWEPT_FACE",FACE,{"disambiguationData":[OSD([subQ0]),TDD([makeQuery(id+"F0.imprint","IMPRINT",EDGE,{"disambiguationData":[TD([[makeQuery(id+"F0.imprint","INTERSECT",VERTEX,{"derivedFrom":[sQuery(id+"F0.wireOp",EDGE,"E1.sketch_text.stroke-30"),subQ0]}),1.0]])],"derivedFrom":subQ0})])]});}
            var Q27;
            {var subQ0=sQuery(id+"F0.wireOp",EDGE,"E3.top");Q27=makeQuery(id+"F2.opExtrude","SWEPT_FACE",FACE,{"disambiguationData":[OSD([subQ0]),TDD([makeQuery(id+"F0.imprint","IMPRINT",EDGE,{"disambiguationData":[TD([[makeQuery(id+"F0.imprint","INTERSECT",VERTEX,{"derivedFrom":[sQuery(id+"F0.wireOp",EDGE,"E0.sketch_text.stroke-27"),subQ0]}),1.0]])],"derivedFrom":subQ0})])]});}
            var Q28;
            {var subQ0=sQuery(id+"F0.wireOp",EDGE,"E3.top");Q28=makeQuery(id+"F2.opExtrude","SWEPT_FACE",FACE,{"disambiguationData":[OSD([subQ0]),TDD([makeQuery(id+"F0.imprint","IMPRINT",EDGE,{"disambiguationData":[TD([[makeQuery(id+"F0.imprint","INTERSECT",VERTEX,{"derivedFrom":[sQuery(id+"F0.wireOp",EDGE,"E0.sketch_text.stroke-0"),subQ0]}),1.0]])],"derivedFrom":subQ0})])]});}
            var Q29;
            {var subQ0=sQuery(id+"F0.wireOp",EDGE,"E3.top");Q29=makeQuery(id+"F2.opExtrude","SWEPT_FACE",FACE,{"disambiguationData":[OSD([subQ0]),TDD([makeQuery(id+"F0.imprint","IMPRINT",EDGE,{"disambiguationData":[TD([[makeQuery(id+"F0.imprint","INTERSECT",VERTEX,{"derivedFrom":[sQuery(id+"F0.wireOp",EDGE,"E0.sketch_text.stroke-17"),subQ0]}),1.0]])],"derivedFrom":subQ0})])]});}
            var Q30;
            Q30=makeQuery(id+"F1.opExtrude","SWEPT_FACE",FACE,{"disambiguationData":[OSD([sQuery(id+"F0.wireOp",EDGE,"E1.sketch_text.stroke-32")])]});
            fillet(context, id + "F6", {"entities" : qUnion([Q0, Q1, Q2, Q3, Q4, Q5, Q6, Q7, Q8, Q9, Q10, Q11, Q12, Q13, Q14, Q15, Q16, Q17, Q18, Q19, Q20, Q21, Q22, Q23, Q24, Q25, Q26, Q27, Q28, Q29, Q30]), "radius" : .5 * mm, "tangentPropagation" : true, "allowEdgeOverflow" : false});
        }
    });
